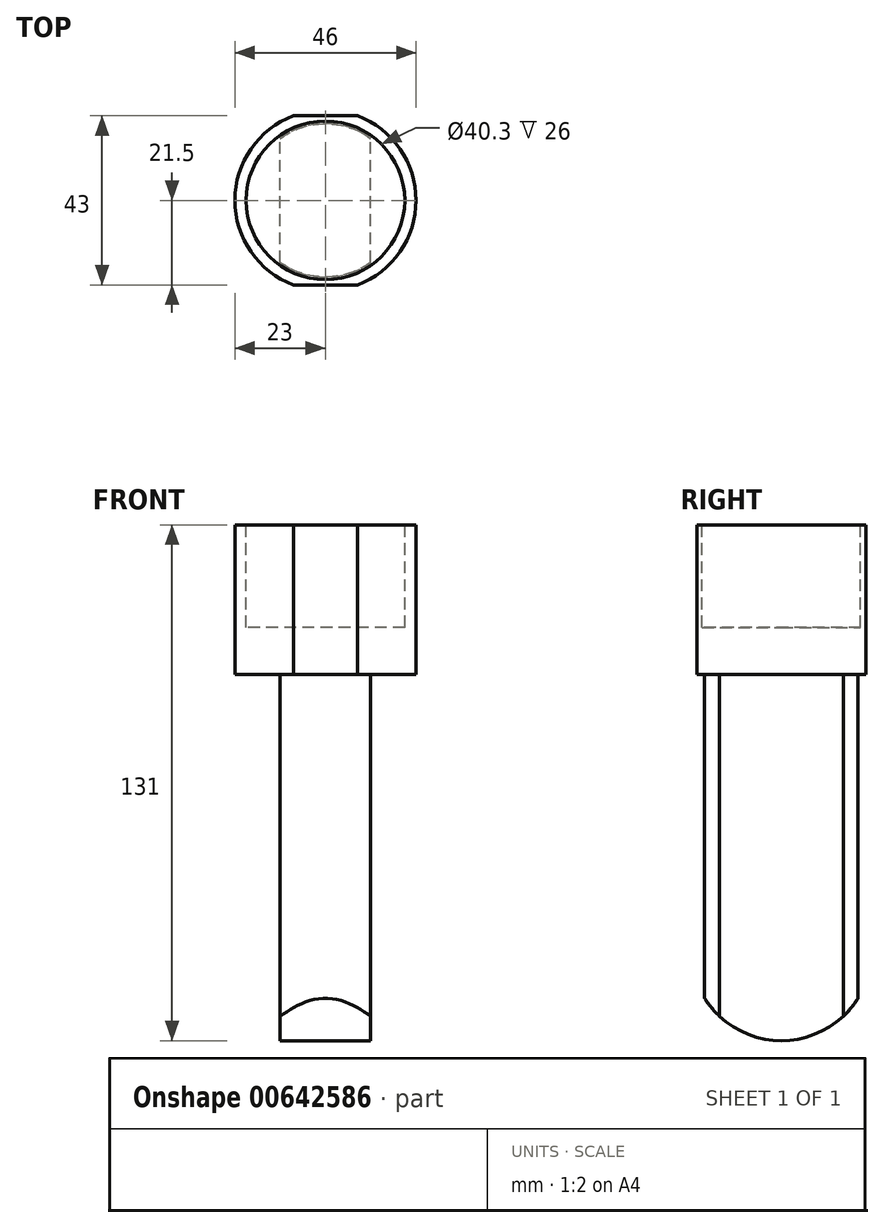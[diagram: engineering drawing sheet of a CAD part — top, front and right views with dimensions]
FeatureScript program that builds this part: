
annotation { "Feature Type Name" : "Feature", "Feature Type Description" : "" }
export const myFeature = defineFeature(function(context is Context, id is Id, definition is map)
    precondition{}
    {
        {
            var Q0;
            Q0=qCreatedBy(makeId("Top.planeOp"),FACE);
            var sketch = newSketch(context, id + "F0", { "sketchPlane" : qUnion([Q0])});
            skArc(sketch, "E0", {"start": v(-8.17, 21.5) * mm, "mid": v(-23, 0) * mm, "end": v(-8.17, -21.5) * mm});
            skLineSegment(sketch, "E1", {"start": v(-8.17, 21.5) * mm, "end": v(8.17, 21.5) * mm});
            skLineSegment(sketch, "E2.MirrorCS", {"start": v(-8.17, -21.5) * mm, "end": v(8.17, -21.5) * mm});
            skArc(sketch, "E3.trimOffspring", {"start": v(8.17, -21.5) * mm, "mid": v(23, 0) * mm, "end": v(8.17, 21.5) * mm});
            skSolve(sketch);
        }
        {
            var Q0;
            Q0=makeQuery(id+"F0.imprint","IMPRINT",FACE,{"disambiguationData":[TD([[makeQuery(id+"F0.imprint","IMPRINT",EDGE,{"derivedFrom":sQuery(id+"F0.wireOp",EDGE,"E0")}),1.0]])]});
            extrude(context, id + "F1", {"entities" : qUnion([Q0]), "depth" : 38 * mm, "offsetDistance" : 25 * mm});
        }
        {
            var Q0;
            Q0=makeQuery(id+"F1.opExtrude","CAP_FACE",FACE,{"disambiguationData":[OSD([sQuery(id+"F0.wireOp",EDGE,"E0"),sQuery(id+"F0.wireOp",EDGE,"E1"),sQuery(id+"F0.wireOp",EDGE,"E2.MirrorCS"),sQuery(id+"F0.wireOp",EDGE,"E3.trimOffspring")])],"isStart":false});
            var sketch = newSketch(context, id + "F2", { "sketchPlane" : qUnion([Q0])});
            skCircle(sketch, "E4", {"center": v(0, 0) * mm, "radius": 20.15 * mm});
            skSolve(sketch);
        }
        {
            var Q0;
            Q0=makeQuery(id+"F2.imprint","IMPRINT",FACE,{"disambiguationData":[TD([[makeQuery(id+"F2.imprint","IMPRINT",EDGE,{"derivedFrom":sQuery(id+"F2.wireOp",EDGE,"E4")}),1.0]])]});
            extrude(context, id + "F3", {"entities" : qUnion([Q0]), "operationType" : NewBodyOperationType.REMOVE, "oppositeDirection" : true, "depth" : 26 * mm, "offsetDistance" : 25 * mm});
        }
        {
            var Q0;
            Q0=makeQuery(id+"F1.opExtrude","CAP_FACE",FACE,{"disambiguationData":[OSD([sQuery(id+"F0.wireOp",EDGE,"E0"),sQuery(id+"F0.wireOp",EDGE,"E1"),sQuery(id+"F0.wireOp",EDGE,"E2.MirrorCS"),sQuery(id+"F0.wireOp",EDGE,"E3.trimOffspring")])],"isStart":true});
            var sketch = newSketch(context, id + "F4", { "sketchPlane" : qUnion([Q0])});
            skArc(sketch, "E5", {"start": v(-11.5, -15.75) * mm, "mid": v(0, -19.5) * mm, "end": v(11.5, -15.75) * mm});
            skLineSegment(sketch, "E6", {"start": v(-11.5, 15.75) * mm, "end": v(-11.5, -15.75) * mm});
            skLineSegment(sketch, "E7.MirrorCS", {"start": v(11.5, 15.75) * mm, "end": v(11.5, -15.75) * mm});
            skArc(sketch, "E8.trimOffspring", {"start": v(11.5, 15.75) * mm, "mid": v(0, 19.5) * mm, "end": v(-11.5, 15.75) * mm});
            skSolve(sketch);
        }
        {
            var Q0;
            Q0=makeQuery(id+"F4.imprint","IMPRINT",FACE,{"disambiguationData":[TD([[makeQuery(id+"F4.imprint","IMPRINT",EDGE,{"derivedFrom":sQuery(id+"F4.wireOp",EDGE,"E5")}),1.0]])]});
            extrude(context, id + "F5", {"entities" : qUnion([Q0]), "operationType" : NewBodyOperationType.ADD, "depth" : 93 * mm, "offsetDistance" : 25 * mm});
        }
        {
            var Q0;
            Q0=makeQuery(id+"F5.opExtrude","SWEPT_FACE",FACE,{"disambiguationData":[OSD([sQuery(id+"F4.wireOp",EDGE,"E7.MirrorCS")])]});
            var sketch = newSketch(context, id + "F6", { "sketchPlane" : qUnion([Q0])});
            skArc(sketch, "E9", {"start": v(-21.68, -77.67) * mm, "mid": v(-0.6, -93) * mm, "end": v(21.26, -78.79) * mm});
            skLineSegment(sketch, "E10", {"start": v(-21.68, -77.67) * mm, "end": v(-46.37, -111.22) * mm});
            skLineSegment(sketch, "E11", {"start": v(-46.37, -111.22) * mm, "end": v(36.25, -100.77) * mm});
            skLineSegment(sketch, "E12", {"start": v(36.25, -100.77) * mm, "end": v(21.26, -78.79) * mm});
            skSolve(sketch);
        }
        {
            var Q0;
            {var subQ0=sQuery(id+"F6.wireOp",EDGE,"E9");var subQ1=sQuery(id+"F4.wireOp",EDGE,"E7.MirrorCS");var subQ4=makeQuery(id+"F5.opExtrude","CAP_EDGE",EDGE,{"disambiguationData":[OSD([subQ1])],"isStart":false});var subQ5=makeQuery(id+"F6.imprint","INTERSECT",VERTEX,{"derivedFrom":[subQ4,subQ0]});Q0=makeQuery(id+"F6.imprint","IMPRINT",FACE,{"disambiguationData":[TD([[makeQuery(id+"F6.imprint","IMPRINT",EDGE,{"disambiguationData":[TD([[subQ5,1.0]])],"derivedFrom":subQ0}),-1.0]])]});}
            var Q1;
            {var subQ0=sQuery(id+"F6.wireOp",EDGE,"E9");var subQ1=sQuery(id+"F4.wireOp",EDGE,"E7.MirrorCS");var subQ4=makeQuery(id+"F5.opExtrude","CAP_EDGE",EDGE,{"disambiguationData":[OSD([subQ1])],"isStart":false});var subQ5=makeQuery(id+"F6.imprint","INTERSECT",VERTEX,{"derivedFrom":[subQ4,subQ0]});Q1=makeQuery(id+"F6.imprint","IMPRINT",FACE,{"disambiguationData":[TD([[makeQuery(id+"F6.imprint","IMPRINT",EDGE,{"disambiguationData":[TD([[subQ5,-1.0]])],"derivedFrom":subQ0}),-1.0]])]});}
            var Q2;
            {var subQ0=sQuery(id+"F6.wireOp",EDGE,"E10");Q2=makeQuery(id+"F6.imprint","IMPRINT",FACE,{"disambiguationData":[TD([[makeQuery(id+"F6.imprint","IMPRINT",EDGE,{"derivedFrom":subQ0}),1.0]])]});}
            extrude(context, id + "F7", {"entities" : qUnion([Q0, Q1, Q2]), "operationType" : NewBodyOperationType.REMOVE, "oppositeDirection" : true, "depth" : 25 * mm, "offsetDistance" : 25 * mm});
        }
    });
